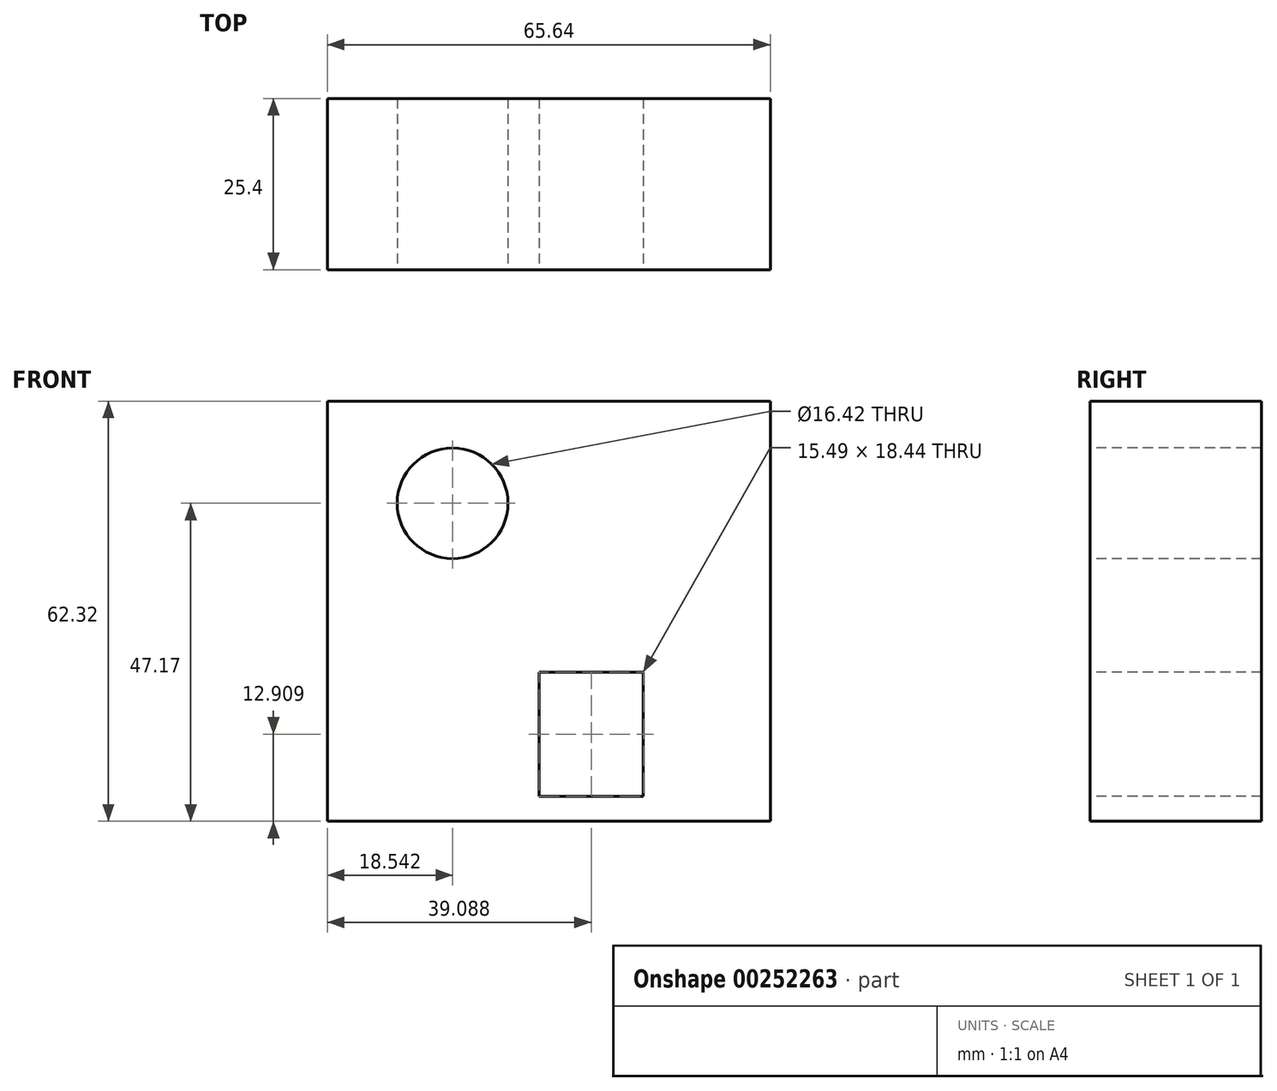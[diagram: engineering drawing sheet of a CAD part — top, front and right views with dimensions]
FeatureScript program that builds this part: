
annotation { "Feature Type Name" : "Feature", "Feature Type Description" : "" }
export const myFeature = defineFeature(function(context is Context, id is Id, definition is map)
    precondition{}
    {
        {
            var Q0;
            Q0=qCreatedBy(makeId("Front.planeOp"),FACE);
            var sketch = newSketch(context, id + "F0", { "sketchPlane" : qUnion([Q0])});
            skLineSegment(sketch, "E0.bottom", {"start": v(32.82, 31.16) * mm, "end": v(-32.82, 31.16) * mm});
            skLineSegment(sketch, "E0.top", {"start": v(32.82, -31.16) * mm, "end": v(-32.82, -31.16) * mm});
            skLineSegment(sketch, "E0.left", {"start": v(32.82, 31.16) * mm, "end": v(32.82, -31.16) * mm});
            skLineSegment(sketch, "E0.right", {"start": v(-32.82, 31.16) * mm, "end": v(-32.82, -31.16) * mm});
            skPoint(sketch, "E0.middle", {"position": v(0, 0) * mm});
            skSolve(sketch);
        }
        {
            var Q0;
            Q0=makeQuery(id+"F0.imprint","IMPRINT",FACE,{"disambiguationData":[TD([[makeQuery(id+"F0.imprint","IMPRINT",EDGE,{"derivedFrom":sQuery(id+"F0.wireOp",EDGE,"E0.bottom")}),1.0]])]});
            extrude(context, id + "F1", {"entities" : qUnion([Q0]), "depth" : 25.4 * mm});
        }
        {
            var Q0;
            Q0=makeQuery(id+"F1.opExtrude","CAP_FACE",FACE,{"disambiguationData":[OSD([sQuery(id+"F0.wireOp",EDGE,"E0.bottom"),sQuery(id+"F0.wireOp",EDGE,"E0.top"),sQuery(id+"F0.wireOp",EDGE,"E0.left"),sQuery(id+"F0.wireOp",EDGE,"E0.right")])],"isStart":false});
            var sketch = newSketch(context, id + "F2", { "sketchPlane" : qUnion([Q0])});
            skCircle(sketch, "E1", {"center": v(-14.28, 16) * mm, "radius": 8.2 * mm});
            skSolve(sketch);
        }
        {
            var Q0;
            Q0=makeQuery(id+"F2.imprint","IMPRINT",FACE,{"disambiguationData":[TD([[makeQuery(id+"F2.imprint","IMPRINT",EDGE,{"derivedFrom":sQuery(id+"F2.wireOp",EDGE,"E1")}),1.0]])]});
            extrude(context, id + "F3", {"entities" : qUnion([Q0]), "operationType" : NewBodyOperationType.REMOVE, "endBound" : BoundingType.THROUGH_ALL, "oppositeDirection" : true, "depth" : 25.4 * mm});
        }
        {
            var Q0;
            Q0=makeQuery(id+"F1.opExtrude","CAP_FACE",FACE,{"disambiguationData":[OSD([sQuery(id+"F0.wireOp",EDGE,"E0.bottom"),sQuery(id+"F0.wireOp",EDGE,"E0.top"),sQuery(id+"F0.wireOp",EDGE,"E0.left"),sQuery(id+"F0.wireOp",EDGE,"E0.right")])],"isStart":false});
            var sketch = newSketch(context, id + "F4", { "sketchPlane" : qUnion([Q0])});
            skLineSegment(sketch, "E2.bottom", {"start": v(14.01, -9.03) * mm, "end": v(-1.47, -9.03) * mm});
            skLineSegment(sketch, "E2.top", {"start": v(14.01, -27.47) * mm, "end": v(-1.47, -27.47) * mm});
            skLineSegment(sketch, "E2.left", {"start": v(14.01, -9.03) * mm, "end": v(14.01, -27.47) * mm});
            skLineSegment(sketch, "E2.right", {"start": v(-1.47, -9.03) * mm, "end": v(-1.47, -27.47) * mm});
            skPoint(sketch, "E2.middle", {"position": v(6.27, -18.25) * mm});
            skSolve(sketch);
        }
        {
            var Q0;
            Q0=makeQuery(id+"F4.imprint","IMPRINT",FACE,{"disambiguationData":[TD([[makeQuery(id+"F4.imprint","IMPRINT",EDGE,{"derivedFrom":sQuery(id+"F4.wireOp",EDGE,"E2.bottom")}),1.0]])]});
            extrude(context, id + "F5", {"entities" : qUnion([Q0]), "operationType" : NewBodyOperationType.REMOVE, "oppositeDirection" : true, "depth" : 25.4 * mm});
        }
    });
